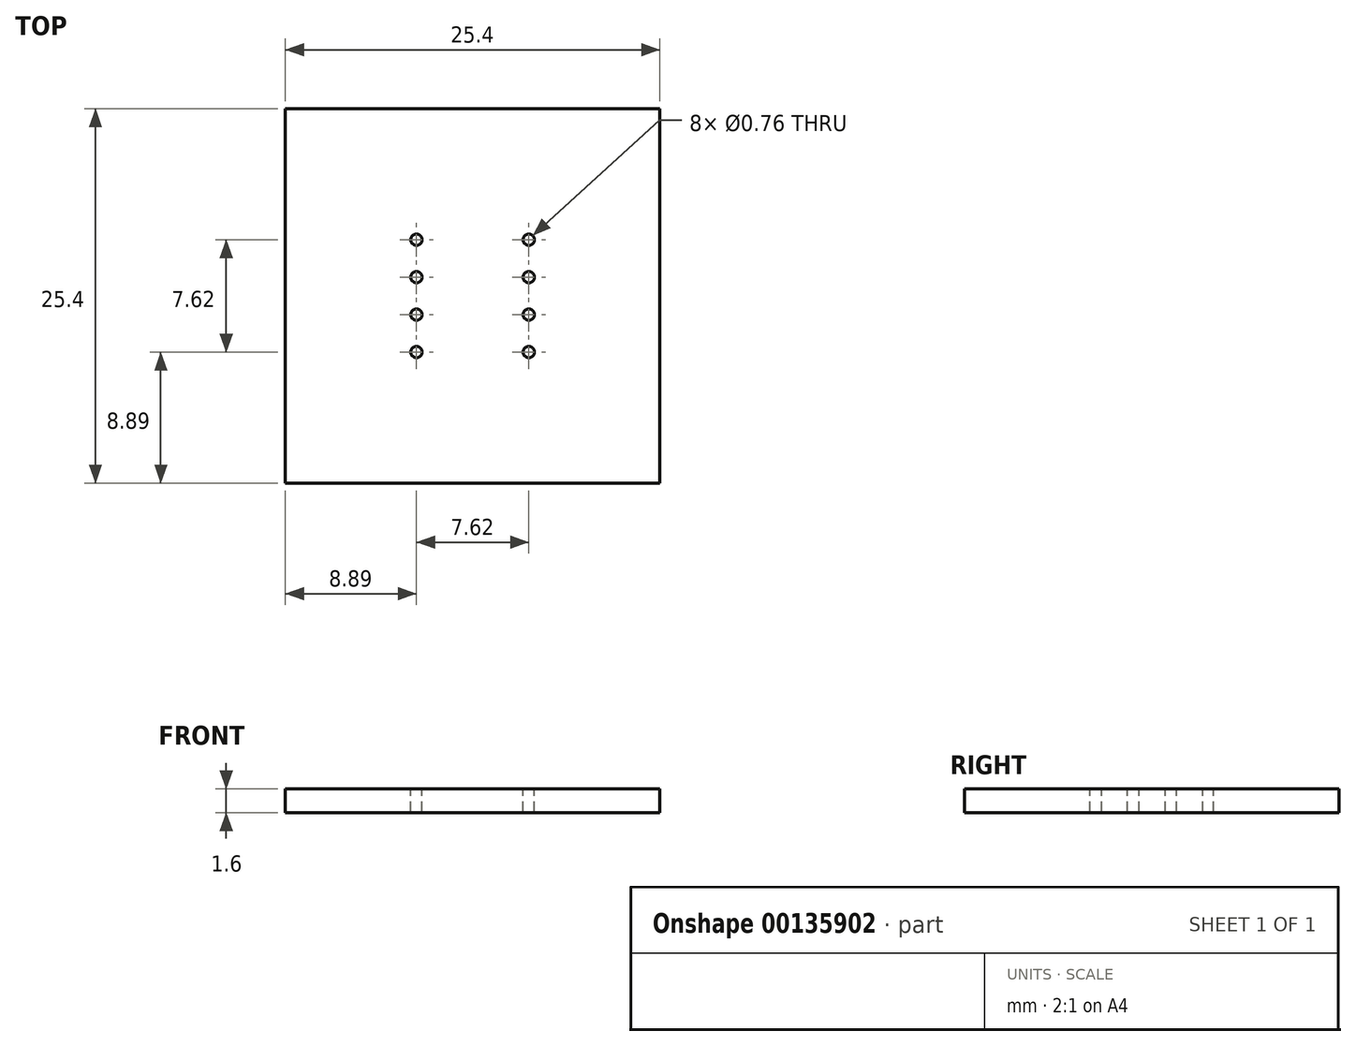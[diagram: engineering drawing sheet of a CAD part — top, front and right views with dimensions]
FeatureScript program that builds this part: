
annotation { "Feature Type Name" : "Feature", "Feature Type Description" : "" }
export const myFeature = defineFeature(function(context is Context, id is Id, definition is map)
    precondition{}
    {
        {
            var Q0;
            Q0=qCreatedBy(makeId("Top.planeOp"),FACE);
            var sketch = newSketch(context, id + "F0", { "sketchPlane" : qUnion([Q0])});
            skLineSegment(sketch, "E0.bottom", {"start": v(-12.7, 12.7) * mm, "end": v(12.7, 12.7) * mm});
            skLineSegment(sketch, "E0.top", {"start": v(-12.7, -12.7) * mm, "end": v(12.7, -12.7) * mm});
            skLineSegment(sketch, "E0.left", {"start": v(-12.7, 12.7) * mm, "end": v(-12.7, -12.7) * mm});
            skLineSegment(sketch, "E0.right", {"start": v(12.7, 12.7) * mm, "end": v(12.7, -12.7) * mm});
            skLineSegment(sketch, "E1", {"start": v(-12.7, -12.7) * mm, "end": v(12.7, 12.7) * mm, "construction": true});
            skSolve(sketch);
        }
        {
            var Q0;
            Q0 = qSketchRegion(id + "F0", true);
            extrude(context, id + "F1", {"entities" : qUnion([Q0]), "oppositeDirection" : true, "depth" : 1.6 * mm});
        }
        {
            var Q0;
            Q0=makeQuery(id+"F1.opExtrude","CAP_FACE",FACE,{"disambiguationData":[OSD([sQuery(id+"F0.wireOp",EDGE,"E0.bottom"),sQuery(id+"F0.wireOp",EDGE,"E0.top"),sQuery(id+"F0.wireOp",EDGE,"E0.left"),sQuery(id+"F0.wireOp",EDGE,"E0.right")])],"isStart":true});
            var sketch = newSketch(context, id + "F2", { "sketchPlane" : qUnion([Q0])});
            skPoint(sketch, "E2", {"position": v(-3.81, 3.8) * mm});
            skPoint(sketch, "E3.0.1.0", {"position": v(-3.81, 1.27) * mm});
            skPoint(sketch, "E3.0.2.0", {"position": v(-3.81, -1.27) * mm});
            skPoint(sketch, "E3.0.3.0", {"position": v(-3.8, -3.81) * mm});
            skPoint(sketch, "E3.1.0.0", {"position": v(3.81, 3.81) * mm});
            skPoint(sketch, "E3.1.1.0", {"position": v(3.81, 1.27) * mm});
            skPoint(sketch, "E3.1.2.0", {"position": v(3.81, -1.27) * mm});
            skPoint(sketch, "E3.1.3.0", {"position": v(3.81, -3.81) * mm});
            skLineSegment(sketch, "E3.direction1", {"start": v(-3.81, 3.81) * mm, "end": v(3.81, 3.81) * mm, "construction": true});
            skLineSegment(sketch, "E3.direction2", {"start": v(-3.81, 3.8) * mm, "end": v(-3.81, 1.27) * mm, "construction": true});
            skLineSegment(sketch, "E4", {"start": v(3.81, 3.81) * mm, "end": v(-3.81, -3.81) * mm, "construction": true});
            skSolve(sketch);
        }
        {
            var Q0;
            Q0=sQuery(id+"F2.wireOp",VERTEX,"E2");
            var Q1;
            Q1=sQuery(id+"F2.wireOp",VERTEX,"E3.0.1.0");
            var Q2;
            Q2=sQuery(id+"F2.wireOp",VERTEX,"E3.0.2.0");
            var Q3;
            Q3=sQuery(id+"F2.wireOp",VERTEX,"E3.0.3.0");
            var Q4;
            Q4=sQuery(id+"F2.wireOp",VERTEX,"E3.1.2.0");
            var Q5;
            Q5=sQuery(id+"F2.wireOp",VERTEX,"E3.1.1.0");
            var Q6;
            Q6=sQuery(id+"F2.wireOp",VERTEX,"E3.1.0.0");
            var Q7;
            Q7=sQuery(id+"F2.wireOp",VERTEX,"E3.1.3.0");
            var Q8;
            Q8=makeQuery(id+"F1.opExtrude","SWEPT_BODY",BODY,{"disambiguationData":[OSD([sQuery(id+"F0.wireOp",EDGE,"E0.bottom"),sQuery(id+"F0.wireOp",EDGE,"E0.top"),sQuery(id+"F0.wireOp",EDGE,"E0.left"),sQuery(id+"F0.wireOp",EDGE,"E0.right")])]});
            hole(context, id + "F3", {"style" : HoleStyle.SIMPLE, "endStyle" : HoleEndStyle.THROUGH, "holeDiameter" : 0.76 * mm, "locations" : qUnion([Q0, Q1, Q2, Q3, Q4, Q5, Q6, Q7]), "scope" : qUnion([Q8]), "isTappedThrough" : true});
        }
    });
